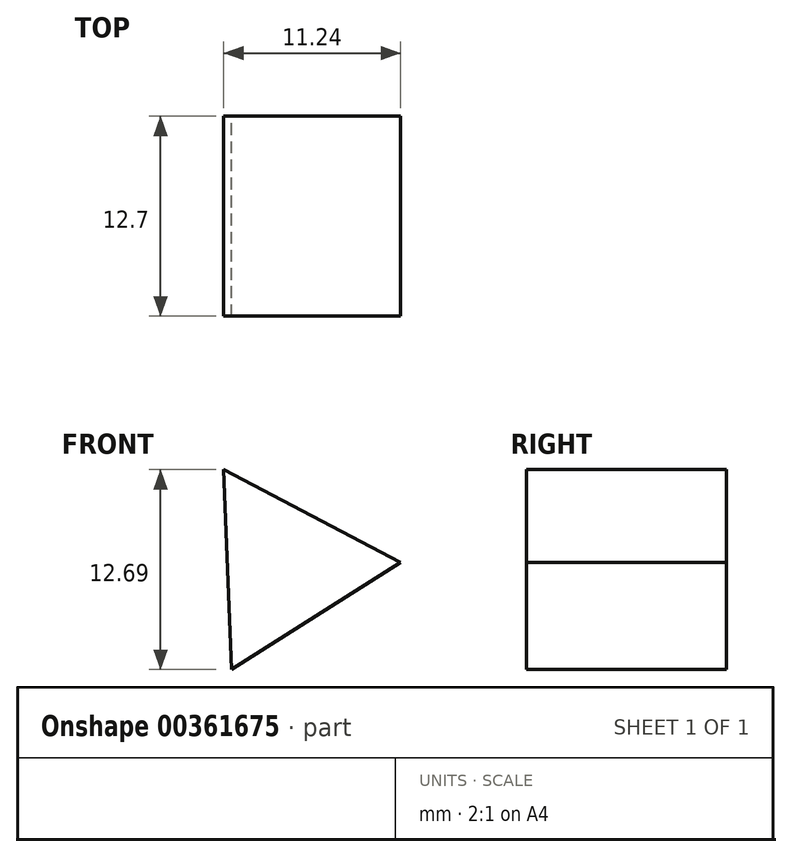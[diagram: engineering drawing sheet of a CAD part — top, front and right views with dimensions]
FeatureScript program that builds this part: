
annotation { "Feature Type Name" : "Feature", "Feature Type Description" : "" }
export const myFeature = defineFeature(function(context is Context, id is Id, definition is map)
    precondition{}
    {
        {
            var Q0;
            Q0=qCreatedBy(makeId("Front.planeOp"),FACE);
            var sketch = newSketch(context, id + "F0", { "sketchPlane" : qUnion([Q0])});
            skCircle(sketch, "E0.cCircle", {"center": v(-37.92, 29.8) * mm, "radius": 3.67 * mm, "construction": true});
            skLineSegment(sketch, "E0.0", {"start": v(-41.83, 36) * mm, "end": v(-30.6, 30.09) * mm});
            skLineSegment(sketch, "E0.1", {"start": v(-30.6, 30.09) * mm, "end": v(-41.34, 23.31) * mm});
            skLineSegment(sketch, "E0.2", {"start": v(-41.34, 23.31) * mm, "end": v(-41.83, 36) * mm});
            skPoint(sketch, "E0.0.midPoint", {"position": v(-36.21, 33.05) * mm});
            skSolve(sketch);
        }
        {
            var Q0;
            Q0=makeQuery(id+"F0.imprint","IMPRINT",FACE,{"disambiguationData":[TD([[makeQuery(id+"F0.imprint","IMPRINT",EDGE,{"derivedFrom":sQuery(id+"F0.wireOp",EDGE,"E0.0")}),-1.0]])]});
            extrude(context, id + "F1", {"entities" : qUnion([Q0]), "depth" : 12.7 * mm});
        }
    });
